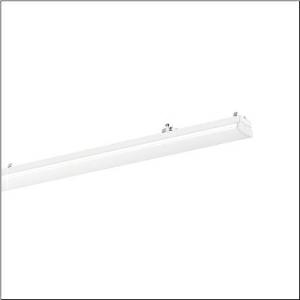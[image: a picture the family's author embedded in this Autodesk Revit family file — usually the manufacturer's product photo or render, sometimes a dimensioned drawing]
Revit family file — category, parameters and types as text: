
# Revit family: licross_11_recessed_opal_mo_51tl1d7n44xg
name_source: partatom
category: Lighting Fixtures
units: mm (PartAtom-declared; Revit-internal decimal feet)

## family parameters
Cut with Voids When Loaded = No
Host = Face
Light Source = No
Part Type = Normal
Room Calculation Point = No
Round Connector Dimension = Use Diameter
Shared = No

## types (1)
- Licross 11 recessed opal MO (1 x LED, 4480 lm, 24.8 W, 4000K)
    Apparent Load = 25 VA
    CIE Flux Codes = 44 73 91 87 100
    Color Rendering = 80
    Color Temperature = 4000K
    Default Elevation = 1800 mm
    Description = Licross 11 recessed opal MO, luminaire insert, of sheet steel, coil coated, white, length: 1.500mm, width: 76mm, height: 87mm, LED rated luminous flux: 4.480lm, light colour: 840, SDCM (Standard Deviation of Colour Matching)MacAdam ≤ 2 SDCM (initial), control gear: ON/OFF, with plug, 3-pole, with phase selection, mains connection: 220..240V, AC, 50/60Hz, rated input power: 25W, internal wiring halogen-free, primary optical cover: cover, of PMMA, light emission: direct with ceiling illumination distribution, primary light characteristic: symmetric, protection rating (complete): IP40, insulation class (complete): insulation class I (protective earthing), certification: CE, ENEC, VDE, UKCA, protection symbol: D if used in an environment without relevant dust loads with corresponding accessories, impact resistance: IK06, permissible ambient temperature for indoor applications: -35..+45°C, corresponds to IFS (International Featured Standards) requirements for safety and quality in the food industry, reducing of maximum allowable ambient temperature of 5°C with ceiling mounting, The light source and the operating device comply with the requirements of the Ecodesign Regulation (EU) 2019/2020 and are replaceable in accordance with this regulation, packaging unit: 1 piece
    Height = 83 mm
    Lamp = 1 x LED
    Lamp Light Flux = 4480 lm
    Lamp Power = 24.8 W
    Lamp count = 1
    Length = 1500 mm
    Luminous efficacy = 181 lm/W
    Manufacturer = Siteco
    ModVariant = No
    Model = 51TL1D7N44XG
    Mounting Place = Ceiling
    Mounting Type = Pendant
    Number of Poles = 1
    OnlyDefault = Yes
    Power Factor = 1
    Product Name = Licross 11 recessed opal MO
    Product group = luminaire insert | ceiling pendant
    ProductGroupID = 901
    Protection Class = Protection class I
    Protection Degree = IP 40
    RLX_Detail_Level = 1
    RLX_Emergency_Light_Flux = 0 lm
    RLX_Emergency_Type = 0
    RLX_Emergency_Type_DB = No
    RlxData = <blob elided: 23429 chars, md5=41220bed>
    Socket = socket
    Standby Power = 0 W
    System Light Flux = 4480 lm
    System Power = 25 W
    Type Comments = Product without accessories
    Type Image = l_1313666.jpg
    URL = http://relux.com
    VarID = ---
    Voltage = 0 V
    Weight = 0.00 kg
    Width = 76 mm

## geometry (parser evidence)
native form markers: Blend x4, Sweep x13
no freeform markers — native parametric forms only
